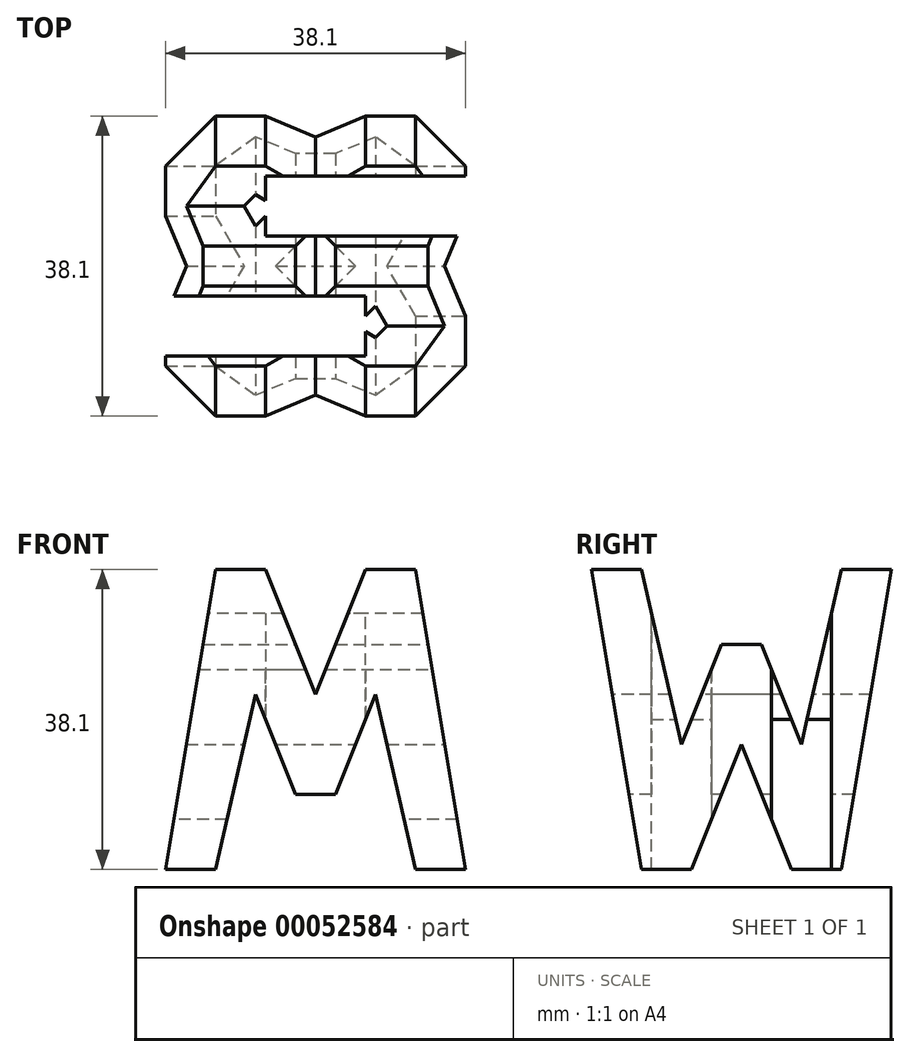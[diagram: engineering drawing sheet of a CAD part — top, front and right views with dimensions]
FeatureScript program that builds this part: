
annotation { "Feature Type Name" : "Feature", "Feature Type Description" : "" }
export const myFeature = defineFeature(function(context is Context, id is Id, definition is map)
    precondition{}
    {
        {
            var Q0;
            Q0=qCreatedBy(makeId("Front.planeOp"),FACE);
            var sketch = newSketch(context, id + "F0", { "sketchPlane" : qUnion([Q0])});
            skLineSegment(sketch, "E0", {"start": v(0, 0) * mm, "end": v(38.1, 0) * mm});
            skLineSegment(sketch, "E1", {"start": v(38.1, 0) * mm, "end": v(38.1, 38.1) * mm});
            skLineSegment(sketch, "E2", {"start": v(38.1, 38.1) * mm, "end": v(0, 38.1) * mm});
            skLineSegment(sketch, "E3", {"start": v(0, 38.1) * mm, "end": v(0, 0) * mm});
            skSolve(sketch);
        }
        {
            var Q0;
            Q0=makeQuery(id+"F0.imprint","IMPRINT",FACE,{"disambiguationData":[TD([[makeQuery(id+"F0.imprint","IMPRINT",EDGE,{"derivedFrom":sQuery(id+"F0.wireOp",EDGE,"E0")}),1.0]])]});
            extrude(context, id + "F1", {"entities" : qUnion([Q0]), "depth" : 38.1 * mm});
        }
        {
            var Q0;
            Q0=qCreatedBy(makeId("Front.planeOp"),FACE);
            cPlane(context, id + "F2", {"entities" : qUnion([Q0]), "cplaneType" : CPlaneType.OFFSET, "offset" : 38.1 * mm, "width" : 152.4 * mm, "height" : 152.4 * mm});
        }
        {
            var Q0;
            Q0=qCreatedBy(makeId("Right.planeOp"),FACE);
            cPlane(context, id + "F3", {"entities" : qUnion([Q0]), "cplaneType" : CPlaneType.OFFSET, "offset" : 38.1 * mm, "width" : 152.4 * mm, "height" : 152.4 * mm});
        }
        {
            var Q0;
            Q0=qCreatedBy(makeId("Top.planeOp"),FACE);
            cPlane(context, id + "F4", {"entities" : qUnion([Q0]), "cplaneType" : CPlaneType.OFFSET, "offset" : 38.1 * mm, "width" : 152.4 * mm, "height" : 152.4 * mm});
        }
        {
            var Q0;
            Q0=qCreatedBy(id+"F3.planeOp",FACE);
            var sketch = newSketch(context, id + "F5", { "sketchPlane" : qUnion([Q0])});
            skLineSegment(sketch, "E4", {"start": v(0, 0) * mm, "end": v(0, 38.1) * mm});
            skLineSegment(sketch, "E5", {"start": v(0, 38.1) * mm, "end": v(-38.1, 38.1) * mm});
            skLineSegment(sketch, "E6", {"start": v(-38.1, 38.1) * mm, "end": v(-38.1, 0) * mm});
            skLineSegment(sketch, "E7", {"start": v(-38.1, 0) * mm, "end": v(0, 0) * mm});
            skLineSegment(sketch, "E8", {"start": v(-38.1, 38.1) * mm, "end": v(-31.75, 0) * mm});
            skLineSegment(sketch, "E9", {"start": v(-31.75, 0) * mm, "end": v(-25.4, 0) * mm});
            skLineSegment(sketch, "E10", {"start": v(-25.4, 0) * mm, "end": v(-19.05, 15.88) * mm});
            skLineSegment(sketch, "E11", {"start": v(-19.05, 15.88) * mm, "end": v(-12.7, 0) * mm});
            skLineSegment(sketch, "E12", {"start": v(-12.7, 0) * mm, "end": v(-6.35, 0) * mm});
            skLineSegment(sketch, "E13", {"start": v(-6.35, 0) * mm, "end": v(0, 38.1) * mm});
            skLineSegment(sketch, "E14", {"start": v(-6.35, 38.1) * mm, "end": v(-11.43, 15.87) * mm});
            skLineSegment(sketch, "E15", {"start": v(-11.43, 15.88) * mm, "end": v(-16.5, 28.58) * mm});
            skLineSegment(sketch, "E16", {"start": v(-16.5, 28.58) * mm, "end": v(-21.59, 28.58) * mm});
            skLineSegment(sketch, "E17", {"start": v(-21.59, 28.58) * mm, "end": v(-26.67, 15.88) * mm});
            skLineSegment(sketch, "E18", {"start": v(-26.67, 15.88) * mm, "end": v(-31.75, 38.1) * mm});
            skSolve(sketch);
        }
        {
            var Q0;
            {var subQ0=sQuery(id+"F5.wireOp",EDGE,"E14");Q0=makeQuery(id+"F5.imprint","IMPRINT",FACE,{"disambiguationData":[TD([[makeQuery(id+"F5.imprint","IMPRINT",EDGE,{"derivedFrom":subQ0}),-1.0]])]});}
            var Q1;
            {var subQ0=sQuery(id+"F5.wireOp",EDGE,"E10");Q1=makeQuery(id+"F5.imprint","IMPRINT",FACE,{"disambiguationData":[TD([[makeQuery(id+"F5.imprint","IMPRINT",EDGE,{"derivedFrom":subQ0}),-1.0]])]});}
            var Q2;
            {var subQ0=sQuery(id+"F5.wireOp",EDGE,"E6");Q2=makeQuery(id+"F5.imprint","IMPRINT",FACE,{"disambiguationData":[TD([[makeQuery(id+"F5.imprint","IMPRINT",EDGE,{"derivedFrom":subQ0}),1.0]])]});}
            var Q3;
            {var subQ0=sQuery(id+"F5.wireOp",EDGE,"E4");Q3=makeQuery(id+"F5.imprint","IMPRINT",FACE,{"disambiguationData":[TD([[makeQuery(id+"F5.imprint","IMPRINT",EDGE,{"derivedFrom":subQ0}),1.0]])]});}
            extrude(context, id + "F6", {"entities" : qUnion([Q0, Q1, Q2, Q3]), "operationType" : NewBodyOperationType.REMOVE, "oppositeDirection" : true, "depth" : 38.1 * mm});
        }
        {
            var Q0;
            Q0=qCreatedBy(id+"F2.planeOp",FACE);
            var sketch = newSketch(context, id + "F7", { "sketchPlane" : qUnion([Q0])});
            skLineSegment(sketch, "E19", {"start": v(0, 38.1) * mm, "end": v(0, 0) * mm});
            skLineSegment(sketch, "E20", {"start": v(0, 0) * mm, "end": v(38.1, 0) * mm});
            skLineSegment(sketch, "E21", {"start": v(38.1, 0) * mm, "end": v(38.1, 38.1) * mm});
            skLineSegment(sketch, "E22", {"start": v(38.1, 38.1) * mm, "end": v(0, 38.1) * mm});
            skLineSegment(sketch, "E23", {"start": v(0, 0) * mm, "end": v(6.35, 38.1) * mm});
            skLineSegment(sketch, "E24", {"start": v(6.35, 38.1) * mm, "end": v(12.7, 38.1) * mm});
            skLineSegment(sketch, "E25", {"start": v(12.7, 38.1) * mm, "end": v(19.05, 22.23) * mm});
            skLineSegment(sketch, "E26", {"start": v(19.05, 22.23) * mm, "end": v(25.4, 38.1) * mm});
            skLineSegment(sketch, "E27", {"start": v(25.4, 38.1) * mm, "end": v(31.75, 38.1) * mm});
            skLineSegment(sketch, "E28", {"start": v(31.75, 38.1) * mm, "end": v(38.1, 0) * mm});
            skLineSegment(sketch, "E29", {"start": v(6.35, 0) * mm, "end": v(11.43, 22.23) * mm});
            skLineSegment(sketch, "E30", {"start": v(11.43, 22.23) * mm, "end": v(16.51, 9.53) * mm});
            skLineSegment(sketch, "E31", {"start": v(16.51, 9.53) * mm, "end": v(21.59, 9.53) * mm});
            skLineSegment(sketch, "E32", {"start": v(21.59, 9.53) * mm, "end": v(26.67, 22.22) * mm});
            skLineSegment(sketch, "E33", {"start": v(26.67, 22.23) * mm, "end": v(31.75, 0) * mm});
            skSolve(sketch);
        }
        {
            var Q0;
            {var subQ0=sQuery(id+"F7.wireOp",EDGE,"E19");Q0=makeQuery(id+"F7.imprint","IMPRINT",FACE,{"disambiguationData":[TD([[makeQuery(id+"F7.imprint","IMPRINT",EDGE,{"derivedFrom":subQ0}),1.0]])]});}
            var Q1;
            {var subQ0=sQuery(id+"F7.wireOp",EDGE,"E29");Q1=makeQuery(id+"F7.imprint","IMPRINT",FACE,{"disambiguationData":[TD([[makeQuery(id+"F7.imprint","IMPRINT",EDGE,{"derivedFrom":subQ0}),-1.0]])]});}
            var Q2;
            {var subQ0=sQuery(id+"F7.wireOp",EDGE,"E25");Q2=makeQuery(id+"F7.imprint","IMPRINT",FACE,{"disambiguationData":[TD([[makeQuery(id+"F7.imprint","IMPRINT",EDGE,{"derivedFrom":subQ0}),1.0]])]});}
            var Q3;
            {var subQ0=sQuery(id+"F7.wireOp",EDGE,"E21");Q3=makeQuery(id+"F7.imprint","IMPRINT",FACE,{"disambiguationData":[TD([[makeQuery(id+"F7.imprint","IMPRINT",EDGE,{"derivedFrom":subQ0}),1.0]])]});}
            extrude(context, id + "F8", {"entities" : qUnion([Q0, Q1, Q2, Q3]), "operationType" : NewBodyOperationType.REMOVE, "oppositeDirection" : true, "depth" : 38.1 * mm});
        }
        {
            var Q0;
            Q0=qCreatedBy(id+"F4.planeOp",FACE);
            var sketch = newSketch(context, id + "F9", { "sketchPlane" : qUnion([Q0])});
            skLineSegment(sketch, "E34", {"start": v(0, 0) * mm, "end": v(38.1, 0) * mm});
            skLineSegment(sketch, "E35", {"start": v(38.1, 0) * mm, "end": v(38.1, -38.1) * mm});
            skLineSegment(sketch, "E36", {"start": v(38.1, -38.1) * mm, "end": v(0, -38.1) * mm});
            skLineSegment(sketch, "E37", {"start": v(0, -38.1) * mm, "end": v(0, 0) * mm});
            skLineSegment(sketch, "E38", {"start": v(38.1, -7.62) * mm, "end": v(12.7, -7.62) * mm});
            skLineSegment(sketch, "E39", {"start": v(12.7, -7.62) * mm, "end": v(12.7, -15.24) * mm});
            skLineSegment(sketch, "E40", {"start": v(12.7, -15.24) * mm, "end": v(38.1, -15.24) * mm});
            skLineSegment(sketch, "E41", {"start": v(0, -22.86) * mm, "end": v(25.4, -22.86) * mm});
            skLineSegment(sketch, "E42", {"start": v(25.4, -22.86) * mm, "end": v(25.4, -30.48) * mm});
            skLineSegment(sketch, "E43", {"start": v(25.4, -30.48) * mm, "end": v(0, -30.48) * mm});
            skSolve(sketch);
        }
        {
            var Q0;
            {var subQ0=sQuery(id+"F9.wireOp",EDGE,"E38");Q0=makeQuery(id+"F9.imprint","IMPRINT",FACE,{"disambiguationData":[TD([[makeQuery(id+"F9.imprint","IMPRINT",EDGE,{"derivedFrom":subQ0}),1.0]])]});}
            var Q1;
            {var subQ0=sQuery(id+"F9.wireOp",EDGE,"E41");Q1=makeQuery(id+"F9.imprint","IMPRINT",FACE,{"disambiguationData":[TD([[makeQuery(id+"F9.imprint","IMPRINT",EDGE,{"derivedFrom":subQ0}),-1.0]])]});}
            extrude(context, id + "F10", {"entities" : qUnion([Q0, Q1]), "operationType" : NewBodyOperationType.REMOVE, "oppositeDirection" : true, "depth" : 38.1 * mm});
        }
    });
